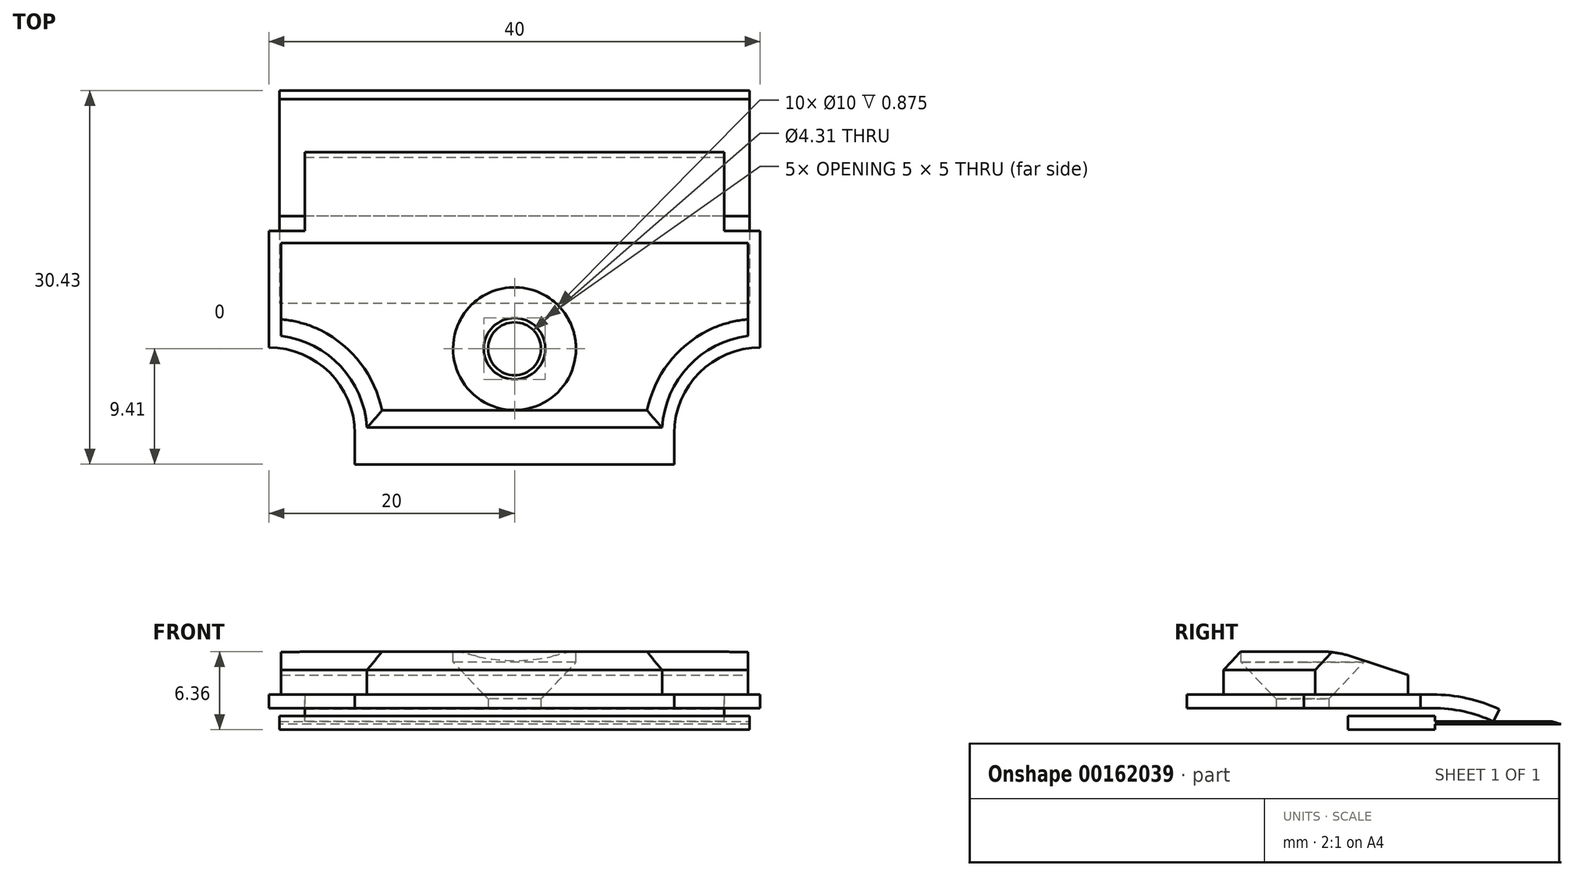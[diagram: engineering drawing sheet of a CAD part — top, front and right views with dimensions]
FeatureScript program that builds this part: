
annotation { "Feature Type Name" : "Feature", "Feature Type Description" : "" }
export const myFeature = defineFeature(function(context is Context, id is Id, definition is map)
    precondition{}
    {
        {
            var Q0;
            Q0=qCreatedBy(makeId("Top.planeOp"),FACE);
            var sketch = newSketch(context, id + "F0", { "sketchPlane" : qUnion([Q0])});
            skLineSegment(sketch, "E0.bottom", {"start": v(-20, 9.6) * mm, "end": v(20, 9.6) * mm});
            skLineSegment(sketch, "E0.left", {"start": v(-20, 9.6) * mm, "end": v(-20, 0.1) * mm});
            skLineSegment(sketch, "E0.right", {"start": v(20, 9.6) * mm, "end": v(20, 0.1) * mm});
            skLineSegment(sketch, "E1", {"start": v(13, -6.9) * mm, "end": v(13, -9.41) * mm});
            skLineSegment(sketch, "E2.MirrorCS", {"start": v(-13, -6.9) * mm, "end": v(-13, -9.41) * mm});
            skArc(sketch, "E3", {"start": v(20, 0.1) * mm, "mid": v(15.05, -1.95) * mm, "end": v(13, -6.9) * mm});
            skArc(sketch, "E4.MirrorCS", {"start": v(-20, 0.1) * mm, "mid": v(-15.05, -1.95) * mm, "end": v(-13, -6.9) * mm});
            skLineSegment(sketch, "E5", {"start": v(-13, -9.41) * mm, "end": v(13, -9.41) * mm});
            skCircle(sketch, "E6", {"center": v(0, 0) * mm, "radius": 2.15 * mm});
            skSolve(sketch);
        }
        {
            var Q0;
            Q0=qSketchRegion(id+"F0",true);
            extrude(context, id + "F1", {"entities" : qUnion([Q0]), "depth" : 1.1 * mm});
        }
        {
            var Q0;
            Q0=qCreatedBy(makeId("Right.planeOp"),FACE);
            var sketch = newSketch(context, id + "F2", { "sketchPlane" : qUnion([Q0])});
            skPoint(sketch, "E7.0", {"position": v(9.6, 0) * mm});
            skPoint(sketch, "E8.0", {"position": v(9.6, 1.1) * mm});
            skLineSegment(sketch, "E9", {"start": v(9.6, 1.1) * mm, "end": v(10.6, 1.1) * mm});
            skLineSegment(sketch, "E10", {"start": v(9.6, 0) * mm, "end": v(10.6, 0) * mm});
            skArc(sketch, "E11", {"start": v(15.54, -1.1) * mm, "mid": v(13.13, -0.28) * mm, "end": v(10.6, 0) * mm});
            skArc(sketch, "E12.0", {"start": v(16.01, -0.1) * mm, "mid": v(13.37, 0.8) * mm, "end": v(10.6, 1.1) * mm});
            skLineSegment(sketch, "E13", {"start": v(16.01, -0.1) * mm, "end": v(15.54, -1.1) * mm});
            skLineSegment(sketch, "E14", {"start": v(9.6, 1.1) * mm, "end": v(9.6, 0) * mm});
            skSolve(sketch);
        }
        {
            var Q0;
            Q0=qSketchRegion(id+"F2",true);
            extrude(context, id + "F3", {"entities" : qUnion([Q0]), "operationType" : NewBodyOperationType.ADD, "depth" : 34.12 * mm, "symmetric" : true});
        }
        {
            var Q0;
            Q0=qCreatedBy(makeId("Right.planeOp"),FACE);
            var sketch = newSketch(context, id + "F4", { "sketchPlane" : qUnion([Q0])});
            skLineSegment(sketch, "E15.bottom", {"start": v(3.69, -1.1) * mm, "end": v(21.6, -1.1) * mm});
            skLineSegment(sketch, "E15.top", {"start": v(3.69, -1.33) * mm, "end": v(21.6, -1.33) * mm});
            skLineSegment(sketch, "E15.left", {"start": v(3.69, -0.66) * mm, "end": v(3.69, -1.76) * mm});
            skLineSegment(sketch, "E15.right", {"start": v(21.6, -1.1) * mm, "end": v(21.6, -1.33) * mm});
            skLineSegment(sketch, "E16", {"start": v(21.6, -1.1) * mm, "end": v(22.61, -1.21) * mm});
            skPoint(sketch, "E16.endSnap0", {"position": v(21.6, -1.21) * mm});
            skLineSegment(sketch, "E17", {"start": v(22.61, -1.21) * mm, "end": v(21.6, -1.33) * mm});
            skLineSegment(sketch, "E18", {"start": v(10.79, -0.66) * mm, "end": v(10.79, -1.76) * mm});
            skLineSegment(sketch, "E19", {"start": v(3.69, -1.21) * mm, "end": v(12.44, -1.21) * mm, "construction": true});
            skLineSegment(sketch, "E20", {"start": v(10.79, -0.66) * mm, "end": v(3.69, -0.66) * mm});
            skLineSegment(sketch, "E21", {"start": v(10.79, -1.76) * mm, "end": v(3.69, -1.76) * mm});
            skSolve(sketch);
        }
        {
            var Q0;
            Q0=qSketchRegion(id+"F4",true);
            extrude(context, id + "F5", {"entities" : qUnion([Q0]), "depth" : 38.25 * mm, "symmetric" : true});
        }
        {
            var Q0;
            Q0=makeQuery(id+"F1.opExtrude","CAP_FACE",FACE,{"disambiguationData":[OSD([sQuery(id+"F0.wireOp",EDGE,"E0.bottom"),sQuery(id+"F0.wireOp",EDGE,"E0.left"),sQuery(id+"F0.wireOp",EDGE,"E0.right"),sQuery(id+"F0.wireOp",EDGE,"E1"),sQuery(id+"F0.wireOp",EDGE,"E2.MirrorCS"),sQuery(id+"F0.wireOp",EDGE,"E3"),sQuery(id+"F0.wireOp",EDGE,"E4.MirrorCS"),sQuery(id+"F0.wireOp",EDGE,"E5"),sQuery(id+"F0.wireOp",EDGE,"E6")])],"isStart":false});
            var sketch = newSketch(context, id + "F6", { "sketchPlane" : qUnion([Q0])});
            skLineSegment(sketch, "E22.0", {"start": v(19, 1.04) * mm, "end": v(19, 8.6) * mm});
            skLineSegment(sketch, "E22.1", {"start": v(-19, 8.6) * mm, "end": v(-19, 1.04) * mm});
            skArc(sketch, "E22.2", {"start": v(-19, 1.04) * mm, "mid": v(-14.16, -1.43) * mm, "end": v(-12.01, -6.42) * mm});
            skLineSegment(sketch, "E22.3", {"start": v(19, 8.6) * mm, "end": v(-19, 8.6) * mm});
            skLineSegment(sketch, "E22.4", {"start": v(-12.01, -6.42) * mm, "end": v(12.01, -6.42) * mm});
            skArc(sketch, "E22.5", {"start": v(12.01, -6.42) * mm, "mid": v(14.16, -1.43) * mm, "end": v(19, 1.04) * mm});
            skCircle(sketch, "E23", {"center": v(0, 0) * mm, "radius": 2.25 * mm});
            skSolve(sketch);
        }
        {
            var Q0;
            Q0=qSketchRegion(id+"F6",true);
            extrude(context, id + "F7", {"entities" : qUnion([Q0]), "depth" : 3.5 * mm});
        }
        {
            var Q0;
            Q0=qCreatedBy(makeId("Front.planeOp"),FACE);
            var sketch = newSketch(context, id + "F8", { "sketchPlane" : qUnion([Q0])});
            skLineSegment(sketch, "E24", {"start": v(0, 0) * mm, "end": v(0, 23.02) * mm, "construction": true});
            skLineSegment(sketch, "E25", {"start": v(0, 3.2) * mm, "end": v(4.5, 3.2) * mm});
            skPoint(sketch, "E26", {"position": v(0, 3.2) * mm});
            skLineSegment(sketch, "E27", {"start": v(-2.5, 1.1) * mm, "end": v(2.5, 1.1) * mm});
            skPoint(sketch, "E28", {"position": v(0, 1.1) * mm});
            skLineSegment(sketch, "E29", {"start": v(2.5, 1.1) * mm, "end": v(4.5, 3.2) * mm});
            skPoint(sketch, "E30", {"position": v(0, 4.4) * mm});
            skArc(sketch, "E31", {"start": v(4.5, 3.2) * mm, "mid": v(2.33, 4.1) * mm, "end": v(0, 4.4) * mm});
            skLineSegment(sketch, "E32", {"start": v(0, 4.4) * mm, "end": v(0, 1.1) * mm});
            skSolve(sketch);
        }
        {
            var Q0;
            {var subQ0=sQuery(id+"F8.wireOp",EDGE,"E25");Q0=makeQuery(id+"F8.imprint","IMPRINT",FACE,{"disambiguationData":[TD([[makeQuery(id+"F8.imprint","IMPRINT",EDGE,{"derivedFrom":subQ0}),1.0]])]});}
            var Q1;
            {var subQ0=sQuery(id+"F8.wireOp",EDGE,"E25");Q1=makeQuery(id+"F8.imprint","IMPRINT",FACE,{"disambiguationData":[TD([[makeQuery(id+"F8.imprint","IMPRINT",EDGE,{"derivedFrom":subQ0}),-1.0]])]});}
            var Q2;
            Q2=sQuery(id+"F8.wireOp",EDGE,"E24");
            revolve(context, id + "F9", {"entities" : qUnion([Q0, Q1]), "axis" : qUnion([Q2]), "revolveType" : RevolveType.FULL});
        }
        {
            var Q0;
            Q0=makeQuery(id+"F9.opRevolve","SWEPT_BODY",BODY,{"disambiguationData":[OSD([sQuery(id+"F8.wireOp",EDGE,"E27"),sQuery(id+"F8.wireOp",EDGE,"E29"),sQuery(id+"F8.wireOp",EDGE,"E31"),sQuery(id+"F8.wireOp",EDGE,"E32")])]});
            var Q1;
            Q1=makeQuery(id+"F7.opExtrude","SWEPT_BODY",BODY,{"disambiguationData":[OSD([sQuery(id+"F6.wireOp",EDGE,"E22.0"),sQuery(id+"F6.wireOp",EDGE,"E22.1"),sQuery(id+"F6.wireOp",EDGE,"E22.2"),sQuery(id+"F6.wireOp",EDGE,"E22.3"),sQuery(id+"F6.wireOp",EDGE,"E22.4"),sQuery(id+"F6.wireOp",EDGE,"E22.5"),sQuery(id+"F6.wireOp",EDGE,"E23")])]});
            booleanBodies(context, id + "F10", {"operationType" : BooleanOperationType.SUBTRACTION, "tools" : qUnion([Q0]), "targets" : qUnion([Q1]), "keepTools" : true});
        }
        {
            var Q0;
            Q0=makeQuery(id+"F7.opExtrude","CAP_FACE",FACE,{"disambiguationData":[OSD([sQuery(id+"F6.wireOp",EDGE,"E22.0"),sQuery(id+"F6.wireOp",EDGE,"E22.1"),sQuery(id+"F6.wireOp",EDGE,"E22.2"),sQuery(id+"F6.wireOp",EDGE,"E22.3"),sQuery(id+"F6.wireOp",EDGE,"E22.4"),sQuery(id+"F6.wireOp",EDGE,"E22.5"),sQuery(id+"F6.wireOp",EDGE,"E23")])],"isStart":false});
            var sketch = newSketch(context, id + "F11", { "sketchPlane" : qUnion([Q0])});
            skCircle(sketch, "E33.0", {"center": v(0, 0) * mm, "radius": 4.5 * mm, "construction": true});
            skCircle(sketch, "E34.0", {"center": v(0, 0) * mm, "radius": 5 * mm});
            skSolve(sketch);
        }
        {
            var Q0;
            Q0=qSketchRegion(id+"F11",true);
            var Q1;
            Q1=makeQuery(id+"F10.opBoolean","COPY",FACE,{"derivedFrom":makeQuery(id+"F9.opRevolve","SWEPT_FACE",FACE,{"disambiguationData":[OSD([sQuery(id+"F8.wireOp",EDGE,"E29")])]})});
            extrude(context, id + "F12", {"entities" : qUnion([Q0]), "operationType" : NewBodyOperationType.REMOVE, "endBound" : BoundingType.UP_TO_SURFACE, "oppositeDirection" : true, "endBoundEntityFace" : qUnion([Q1]), "depth" : 25 * mm});
        }
        {
            var Q0;
            Q0=qCreatedBy(makeId("Right.planeOp"),FACE);
            var sketch = newSketch(context, id + "F13", { "sketchPlane" : qUnion([Q0])});
            skLineSegment(sketch, "E35", {"start": v(22.69, -1.87) * mm, "end": v(2.31, 4.74) * mm});
            skLineSegment(sketch, "E36", {"start": v(2.31, 4.74) * mm, "end": v(22.69, 4.74) * mm});
            skLineSegment(sketch, "E37", {"start": v(22.69, 4.74) * mm, "end": v(22.69, -1.87) * mm});
            skSolve(sketch);
        }
        {
            var Q0;
            Q0=qSketchRegion(id+"F13",true);
            extrude(context, id + "F14", {"entities" : qUnion([Q0]), "operationType" : NewBodyOperationType.REMOVE, "depth" : 40 * mm, "symmetric" : true});
        }
        {
            var Q0;
            Q0=makeQuery(id+"F14.boolean.opBoolean","INTERSECT",EDGE,{"disambiguationData":[OD(1.0)],"derivedFrom":[makeQuery(id+"F7.opExtrude","CAP_FACE",FACE,{"disambiguationData":[OSD([sQuery(id+"F6.wireOp",EDGE,"E22.0"),sQuery(id+"F6.wireOp",EDGE,"E22.1"),sQuery(id+"F6.wireOp",EDGE,"E22.2"),sQuery(id+"F6.wireOp",EDGE,"E22.3"),sQuery(id+"F6.wireOp",EDGE,"E22.4"),sQuery(id+"F6.wireOp",EDGE,"E22.5"),sQuery(id+"F6.wireOp",EDGE,"E23")])],"isStart":false}),makeQuery(id+"F14.opExtrude","SWEPT_FACE",FACE,{"disambiguationData":[OSD([sQuery(id+"F13.wireOp",EDGE,"E35")])]})]});
            var Q1;
            Q1=makeQuery(id+"F14.boolean.opBoolean","INTERSECT",EDGE,{"disambiguationData":[OD(0.0)],"derivedFrom":[makeQuery(id+"F7.opExtrude","CAP_FACE",FACE,{"disambiguationData":[OSD([sQuery(id+"F6.wireOp",EDGE,"E22.0"),sQuery(id+"F6.wireOp",EDGE,"E22.1"),sQuery(id+"F6.wireOp",EDGE,"E22.2"),sQuery(id+"F6.wireOp",EDGE,"E22.3"),sQuery(id+"F6.wireOp",EDGE,"E22.4"),sQuery(id+"F6.wireOp",EDGE,"E22.5"),sQuery(id+"F6.wireOp",EDGE,"E23")])],"isStart":false}),makeQuery(id+"F14.opExtrude","SWEPT_FACE",FACE,{"disambiguationData":[OSD([sQuery(id+"F13.wireOp",EDGE,"E35")])]})]});
            fillet(context, id + "F15", {"entities" : qUnion([Q0, Q1]), "radius" : 8 * mm, "tangentPropagation" : true, "allowEdgeOverflow" : false});
        }
        {
            var Q0;
            Q0=makeQuery(id+"F7.opExtrude","CAP_EDGE",EDGE,{"disambiguationData":[OSD([sQuery(id+"F6.wireOp",EDGE,"E22.4")])],"isStart":false});
            var Q1;
            Q1=makeQuery(id+"F7.opExtrude","CAP_EDGE",EDGE,{"disambiguationData":[OSD([sQuery(id+"F6.wireOp",EDGE,"E22.5")])],"isStart":false});
            var Q2;
            Q2=makeQuery(id+"F7.opExtrude","CAP_EDGE",EDGE,{"disambiguationData":[OSD([sQuery(id+"F6.wireOp",EDGE,"E22.2")])],"isStart":false});
            chamfer(context, id + "F16", {"entities" : qUnion([Q0, Q1, Q2]), "chamferType" : ChamferType.TWO_OFFSETS, "width1" : 1.4 * mm, "oppositeDirection" : false, "width2" : 1.5 * mm, "tangentPropagation" : true});
        }
    });
